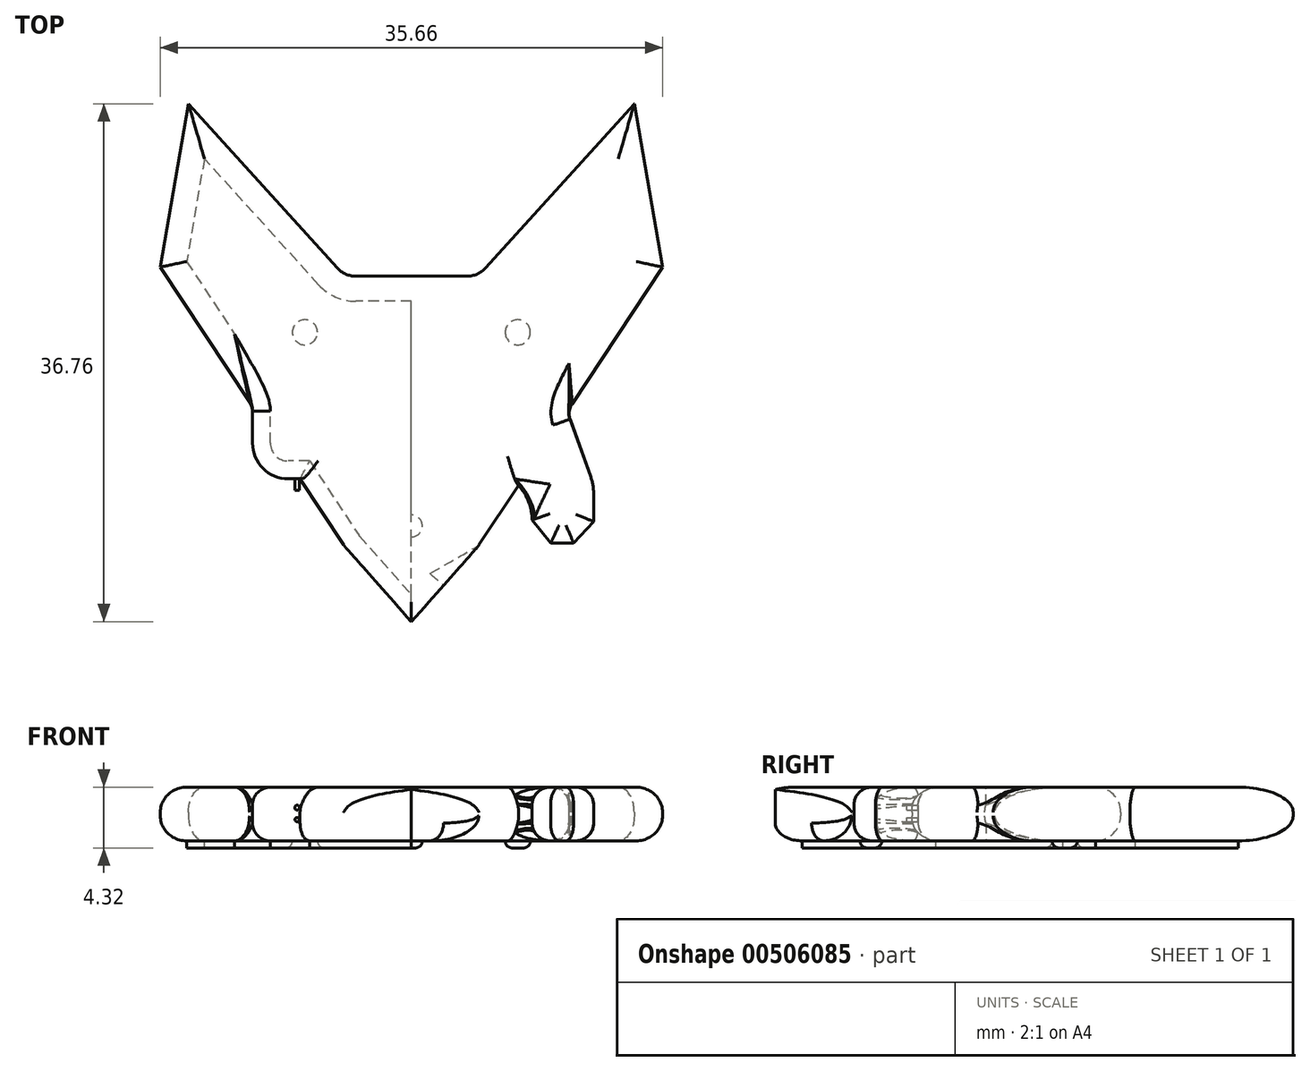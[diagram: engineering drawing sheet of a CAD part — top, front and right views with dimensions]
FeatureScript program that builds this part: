
annotation { "Feature Type Name" : "Feature", "Feature Type Description" : "" }
export const myFeature = defineFeature(function(context is Context, id is Id, definition is map)
    precondition{}
    {
        {
            var Q0;
            Q0=qCreatedBy(makeId("Top.planeOp"),FACE);
            var sketch = newSketch(context, id + "F0", { "sketchPlane" : qUnion([Q0])});
            skLineSegment(sketch, "E0.bottom", {"start": v(4.73, -9.6) * mm, "end": v(-4.73, -9.6) * mm});
            skLineSegment(sketch, "E0.top", {"start": v(4.73, 9.6) * mm, "end": v(-4.73, 9.6) * mm});
            skLineSegment(sketch, "E0.left", {"start": v(4.73, -9.6) * mm, "end": v(4.73, 9.6) * mm});
            skLineSegment(sketch, "E0.right", {"start": v(-4.73, -9.6) * mm, "end": v(-4.73, 9.6) * mm});
            skPoint(sketch, "E0.middle", {"position": v(0, 0) * mm});
            skLineSegment(sketch, "E1", {"start": v(-4.73, 9.6) * mm, "end": v(-15.82, 21.83) * mm});
            skLineSegment(sketch, "E2", {"start": v(-15.82, 21.83) * mm, "end": v(-17.83, 10.24) * mm});
            skLineSegment(sketch, "E3", {"start": v(-17.83, 10.24) * mm, "end": v(-4.73, -9.6) * mm});
            skLineSegment(sketch, "E4", {"start": v(-7.9, -4.79) * mm, "end": v(-11.28, -4.79) * mm});
            skPoint(sketch, "E4.endSnap0", {"position": v(-11.28, 0.33) * mm});
            skLineSegment(sketch, "E5", {"start": v(-11.28, -4.79) * mm, "end": v(-11.28, 0.33) * mm});
            skLineSegment(sketch, "E6", {"start": v(0, 17.28) * mm, "end": v(0, -14.93) * mm});
            skPoint(sketch, "E6.endSnap0", {"position": v(0, 9.6) * mm});
            skLineSegment(sketch, "E7.MirrorCS", {"start": v(4.73, 9.6) * mm, "end": v(15.82, 21.83) * mm});
            skLineSegment(sketch, "E8.MirrorCS", {"start": v(15.82, 21.83) * mm, "end": v(17.83, 10.24) * mm});
            skLineSegment(sketch, "E9.MirrorCS", {"start": v(17.83, 10.24) * mm, "end": v(4.73, -9.6) * mm});
            skCircle(sketch, "E10", {"center": v(0, -9.6) * mm, "radius": 4.73 * mm});
            skLineSegment(sketch, "E11", {"start": v(-4.73, -9.6) * mm, "end": v(0, -14.93) * mm});
            skLineSegment(sketch, "E12", {"start": v(0, -14.93) * mm, "end": v(4.73, -9.6) * mm});
            skLineSegment(sketch, "E13", {"start": v(11.06, 0) * mm, "end": v(12.94, -5.23) * mm});
            skLineSegment(sketch, "E14", {"start": v(12.94, -5.23) * mm, "end": v(12.94, -7.82) * mm});
            skLineSegment(sketch, "E15", {"start": v(12.94, -7.82) * mm, "end": v(11.52, -9.35) * mm});
            skLineSegment(sketch, "E16", {"start": v(11.52, -9.35) * mm, "end": v(9.88, -9.35) * mm});
            skLineSegment(sketch, "E17", {"start": v(9.88, -9.35) * mm, "end": v(8.57, -7.71) * mm});
            skLineSegment(sketch, "E18", {"start": v(8.57, -7.71) * mm, "end": v(8.57, -5.86) * mm});
            skLineSegment(sketch, "E19", {"start": v(8.57, -5.86) * mm, "end": v(7.61, -5.22) * mm});
            skSolve(sketch);
        }
        {
            var Q0;
            {var subQ0=sQuery(id+"F0.wireOp",EDGE,"E10");var subQ3=sQuery(id+"F0.wireOp",EDGE,"E6");var subQ5=makeQuery(id+"F0.imprint","INTERSECT",VERTEX,{"disambiguationData":[OD(0.0)],"derivedFrom":[subQ3,subQ0]});Q0=makeQuery(id+"F0.imprint","IMPRINT",FACE,{"disambiguationData":[TD([[makeQuery(id+"F0.imprint","IMPRINT",EDGE,{"disambiguationData":[TD([[subQ5,1.0]])],"derivedFrom":subQ3}),1.0]])]});}
            var Q1;
            {var subQ0=sQuery(id+"F0.wireOp",EDGE,"E10");var subQ3=sQuery(id+"F0.wireOp",EDGE,"E6");var subQ5=makeQuery(id+"F0.imprint","INTERSECT",VERTEX,{"disambiguationData":[OD(0.0)],"derivedFrom":[subQ3,subQ0]});Q1=makeQuery(id+"F0.imprint","IMPRINT",FACE,{"disambiguationData":[TD([[makeQuery(id+"F0.imprint","IMPRINT",EDGE,{"disambiguationData":[TD([[subQ5,1.0]])],"derivedFrom":subQ3}),-1.0]])]});}
            var Q2;
            {var subQ1=sQuery(id+"F0.wireOp",EDGE,"E0.bottom");var subQ3=sQuery(id+"F0.wireOp",EDGE,"E6");var subQ4=makeQuery(id+"F0.imprint","INTERSECT",VERTEX,{"derivedFrom":[subQ1,subQ3]});Q2=makeQuery(id+"F0.imprint","IMPRINT",FACE,{"disambiguationData":[TD([[makeQuery(id+"F0.imprint","IMPRINT",EDGE,{"disambiguationData":[TD([[subQ4,1.0]])],"derivedFrom":subQ3}),1.0]])]});}
            var Q3;
            {var subQ1=sQuery(id+"F0.wireOp",EDGE,"E0.bottom");var subQ3=sQuery(id+"F0.wireOp",EDGE,"E6");var subQ4=makeQuery(id+"F0.imprint","INTERSECT",VERTEX,{"derivedFrom":[subQ1,subQ3]});Q3=makeQuery(id+"F0.imprint","IMPRINT",FACE,{"disambiguationData":[TD([[makeQuery(id+"F0.imprint","IMPRINT",EDGE,{"disambiguationData":[TD([[subQ4,1.0]])],"derivedFrom":subQ3}),-1.0]])]});}
            var Q4;
            {var subQ0=sQuery(id+"F0.wireOp",EDGE,"E0.left");Q4=makeQuery(id+"F0.imprint","IMPRINT",FACE,{"disambiguationData":[TD([[makeQuery(id+"F0.imprint","IMPRINT",EDGE,{"derivedFrom":subQ0}),1.0]])]});}
            var Q5;
            {var subQ0=sQuery(id+"F0.wireOp",EDGE,"E0.right");Q5=makeQuery(id+"F0.imprint","IMPRINT",FACE,{"disambiguationData":[TD([[makeQuery(id+"F0.imprint","IMPRINT",EDGE,{"derivedFrom":subQ0}),-1.0]])]});}
            var Q6;
            {var subQ3=sQuery(id+"F0.wireOp",EDGE,"E0.right");Q6=makeQuery(id+"F0.imprint","IMPRINT",FACE,{"disambiguationData":[TD([[makeQuery(id+"F0.imprint","IMPRINT",EDGE,{"derivedFrom":subQ3}),1.0]])]});}
            var Q7;
            Q7=makeQuery(id+"F0.imprint","IMPRINT",FACE,{"disambiguationData":[TD([[makeQuery(id+"F0.imprint","IMPRINT",EDGE,{"derivedFrom":sQuery(id+"F0.wireOp",EDGE,"E0.left")}),-1.0]])]});
            var Q8;
            {var subQ2=sQuery(id+"F0.wireOp",EDGE,"E0.bottom");var subQ4=sQuery(id+"F0.wireOp",EDGE,"E6");var subQ5=makeQuery(id+"F0.imprint","INTERSECT",VERTEX,{"derivedFrom":[subQ2,subQ4]});Q8=makeQuery(id+"F0.imprint","IMPRINT",FACE,{"disambiguationData":[TD([[makeQuery(id+"F0.imprint","IMPRINT",EDGE,{"disambiguationData":[TD([[subQ5,-1.0]])],"derivedFrom":subQ4}),-1.0]])]});}
            var Q9;
            {var subQ2=sQuery(id+"F0.wireOp",EDGE,"E0.bottom");var subQ4=sQuery(id+"F0.wireOp",EDGE,"E6");var subQ5=makeQuery(id+"F0.imprint","INTERSECT",VERTEX,{"derivedFrom":[subQ2,subQ4]});Q9=makeQuery(id+"F0.imprint","IMPRINT",FACE,{"disambiguationData":[TD([[makeQuery(id+"F0.imprint","IMPRINT",EDGE,{"disambiguationData":[TD([[subQ5,-1.0]])],"derivedFrom":subQ4}),1.0]])]});}
            var Q10;
            {var subQ0=sQuery(id+"F0.wireOp",EDGE,"E12");var subQ3=sQuery(id+"F0.wireOp",EDGE,"E10");var subQ5=makeQuery(id+"F0.imprint","INTERSECT",VERTEX,{"derivedFrom":[subQ3,subQ0]});Q10=makeQuery(id+"F0.imprint","IMPRINT",FACE,{"disambiguationData":[TD([[makeQuery(id+"F0.imprint","IMPRINT",EDGE,{"disambiguationData":[TD([[subQ5,1.0]])],"derivedFrom":subQ3}),-1.0]])]});}
            var Q11;
            {var subQ0=sQuery(id+"F0.wireOp",EDGE,"E11");var subQ3=sQuery(id+"F0.wireOp",EDGE,"E10");var subQ5=makeQuery(id+"F0.imprint","INTERSECT",VERTEX,{"derivedFrom":[subQ3,subQ0]});Q11=makeQuery(id+"F0.imprint","IMPRINT",FACE,{"disambiguationData":[TD([[makeQuery(id+"F0.imprint","IMPRINT",EDGE,{"disambiguationData":[TD([[subQ5,-1.0]])],"derivedFrom":subQ3}),-1.0]])]});}
            var Q12;
            {var subQ0=sQuery(id+"F0.wireOp",EDGE,"E13");Q12=makeQuery(id+"F0.imprint","IMPRINT",FACE,{"disambiguationData":[TD([[makeQuery(id+"F0.imprint","IMPRINT",EDGE,{"derivedFrom":subQ0}),-1.0]])]});}
            extrude(context, id + "F1", {"entities" : qUnion([Q0, Q1, Q2, Q3, Q4, Q5, Q6, Q7, Q8, Q9, Q10, Q11, Q12]), "depth" : 3.8 * mm});
        }
        {
            var Q0;
            {var subQ0=sQuery(id+"F0.wireOp",EDGE,"E4");Q0=makeQuery(id+"F0.imprint","IMPRINT",FACE,{"disambiguationData":[TD([[makeQuery(id+"F0.imprint","IMPRINT",EDGE,{"derivedFrom":subQ0}),-1.0]])]});}
            extrude(context, id + "F2", {"entities" : qUnion([Q0]), "operationType" : NewBodyOperationType.ADD, "depth" : 3.8 * mm});
        }
        {
            var Q0;
            Q0=makeQuery(id+"F1.opExtrude","CAP_EDGE",EDGE,{"disambiguationData":[OSD([sQuery(id+"F0.wireOp",EDGE,"E0.top")])],"isStart":false});
            var Q1;
            Q1=makeQuery(id+"F1.opExtrude","CAP_EDGE",EDGE,{"disambiguationData":[OSD([sQuery(id+"F0.wireOp",EDGE,"E0.top")])],"isStart":true});
            var Q2;
            Q2=makeQuery(id+"F1.opExtrude","CAP_EDGE",EDGE,{"disambiguationData":[OSD([sQuery(id+"F0.wireOp",EDGE,"E1")])],"isStart":false});
            var Q3;
            Q3=makeQuery(id+"F1.opExtrude","CAP_EDGE",EDGE,{"disambiguationData":[OSD([sQuery(id+"F0.wireOp",EDGE,"E1")])],"isStart":true});
            var Q4;
            Q4=makeQuery(id+"F1.opExtrude","CAP_EDGE",EDGE,{"disambiguationData":[OSD([sQuery(id+"F0.wireOp",EDGE,"E7.MirrorCS")])],"isStart":false});
            var Q5;
            Q5=makeQuery(id+"F1.opExtrude","CAP_EDGE",EDGE,{"disambiguationData":[OSD([sQuery(id+"F0.wireOp",EDGE,"E7.MirrorCS")])],"isStart":true});
            var Q6;
            Q6=makeQuery(id+"F1.opExtrude","CAP_EDGE",EDGE,{"disambiguationData":[OSD([sQuery(id+"F0.wireOp",EDGE,"E2")])],"isStart":false});
            var Q7;
            Q7=makeQuery(id+"F1.opExtrude","CAP_EDGE",EDGE,{"disambiguationData":[OSD([sQuery(id+"F0.wireOp",EDGE,"E2")])],"isStart":true});
            var Q8;
            Q8=makeQuery(id+"F1.opExtrude","CAP_EDGE",EDGE,{"disambiguationData":[OSD([sQuery(id+"F0.wireOp",EDGE,"E3")])],"isStart":false});
            var Q9;
            {var subQ1=sQuery(id+"F0.wireOp",EDGE,"E3");var subQ2=sQuery(id+"F0.wireOp",EDGE,"E2");Q9=makeQuery(id+"F2.boolean.opBoolean","SPLIT",EDGE,{"disambiguationData":[TD([makeQuery(id+"F1.opExtrude","SWEPT_FACE",FACE,{"disambiguationData":[OSD([subQ2])]})])],"derivedFrom":makeQuery(id+"F1.opExtrude","CAP_EDGE",EDGE,{"disambiguationData":[OSD([subQ1])],"isStart":true})});}
            var Q10;
            {var subQ1=sQuery(id+"F0.wireOp",EDGE,"E3");var subQ2=sQuery(id+"F0.wireOp",EDGE,"E10");Q10=makeQuery(id+"F2.boolean.opBoolean","SPLIT",EDGE,{"disambiguationData":[TD([makeQuery(id+"F1.opExtrude","SWEPT_FACE",FACE,{"disambiguationData":[OSD([subQ2])]})])],"derivedFrom":makeQuery(id+"F1.opExtrude","CAP_EDGE",EDGE,{"disambiguationData":[OSD([subQ1])],"isStart":true})});}
            var Q11;
            Q11=makeQuery(id+"F1.opExtrude","CAP_EDGE",EDGE,{"disambiguationData":[OSD([sQuery(id+"F0.wireOp",EDGE,"E9.MirrorCS")])],"isStart":false});
            var Q12;
            Q12=makeQuery(id+"F1.opExtrude","CAP_EDGE",EDGE,{"disambiguationData":[OSD([sQuery(id+"F0.wireOp",EDGE,"E9.MirrorCS")])],"isStart":true});
            var Q13;
            Q13=makeQuery(id+"F1.opExtrude","CAP_EDGE",EDGE,{"disambiguationData":[OSD([sQuery(id+"F0.wireOp",EDGE,"E8.MirrorCS")])],"isStart":false});
            var Q14;
            Q14=makeQuery(id+"F1.opExtrude","CAP_EDGE",EDGE,{"disambiguationData":[OSD([sQuery(id+"F0.wireOp",EDGE,"E8.MirrorCS")])],"isStart":true});
            var Q15;
            Q15=makeQuery(id+"F1.opExtrude","SWEPT_EDGE",EDGE,{"disambiguationData":[OSD([sQuery(id+"F0.wireOp",EDGE,"E0.top"),sQuery(id+"F0.wireOp",EDGE,"E0.right"),sQuery(id+"F0.wireOp",EDGE,"E1")])]});
            var Q16;
            Q16=makeQuery(id+"F1.opExtrude","SWEPT_EDGE",EDGE,{"disambiguationData":[OSD([sQuery(id+"F0.wireOp",EDGE,"E0.top"),sQuery(id+"F0.wireOp",EDGE,"E0.left"),sQuery(id+"F0.wireOp",EDGE,"E7.MirrorCS")])]});
            var Q17;
            Q17=makeQuery(id+"F1.opExtrude","SWEPT_EDGE",EDGE,{"disambiguationData":[OSD([sQuery(id+"F0.wireOp",EDGE,"E0.bottom"),sQuery(id+"F0.wireOp",EDGE,"E0.left"),sQuery(id+"F0.wireOp",EDGE,"E9.MirrorCS"),sQuery(id+"F0.wireOp",EDGE,"E10")])]});
            var Q18;
            Q18=makeQuery(id+"F1.opExtrude","SWEPT_EDGE",EDGE,{"disambiguationData":[OSD([sQuery(id+"F0.wireOp",EDGE,"E0.bottom"),sQuery(id+"F0.wireOp",EDGE,"E0.right"),sQuery(id+"F0.wireOp",EDGE,"E3"),sQuery(id+"F0.wireOp",EDGE,"E10")])]});
            fillet(context, id + "F3", {"entities" : qUnion([Q0, Q1, Q2, Q3, Q4, Q5, Q6, Q7, Q8, Q9, Q10, Q11, Q12, Q13, Q14, Q15, Q16, Q17, Q18]), "radius" : 1.78 * mm, "tangentPropagation" : true, "allowEdgeOverflow" : false});
        }
        {
            var Q0;
            Q0=makeQuery(id+"F2.opExtrude","SWEPT_EDGE",EDGE,{"disambiguationData":[OSD([sQuery(id+"F0.wireOp",EDGE,"E4"),sQuery(id+"F0.wireOp",EDGE,"E5")])]});
            fillet(context, id + "F4", {"entities" : qUnion([Q0]), "radius" : 2.54 * mm, "tangentPropagation" : true, "allowEdgeOverflow" : false});
        }
        {
            var Q0;
            Q0=makeQuery(id+"F2.opExtrude","CAP_EDGE",EDGE,{"disambiguationData":[OSD([sQuery(id+"F0.wireOp",EDGE,"E5")])],"isStart":false});
            var Q1;
            Q1=makeQuery(id+"F2.opExtrude","CAP_EDGE",EDGE,{"disambiguationData":[OSD([sQuery(id+"F0.wireOp",EDGE,"E5")])],"isStart":true});
            var Q2;
            Q2=makeQuery(id+"F2.opExtrude","CAP_EDGE",EDGE,{"disambiguationData":[OSD([sQuery(id+"F0.wireOp",EDGE,"E5")])],"isStart":true});
            var Q3;
            Q3=makeQuery(id+"F2.opExtrude","CAP_EDGE",EDGE,{"disambiguationData":[OSD([sQuery(id+"F0.wireOp",EDGE,"E4")])],"isStart":false});
            var Q4;
            Q4=makeQuery(id+"F2.opExtrude","SWEPT_EDGE",EDGE,{"disambiguationData":[OSD([sQuery(id+"F0.wireOp",EDGE,"E3"),sQuery(id+"F0.wireOp",EDGE,"E5")])]});
            var Q5;
            Q5=makeQuery(id+"F2.opExtrude","SWEPT_EDGE",EDGE,{"disambiguationData":[OSD([sQuery(id+"F0.wireOp",EDGE,"E3"),sQuery(id+"F0.wireOp",EDGE,"E4")])]});
            var Q6;
            Q6=makeQuery(id+"F2.opExtrude","CAP_EDGE",EDGE,{"disambiguationData":[OSD([sQuery(id+"F0.wireOp",EDGE,"E4")])],"isStart":true});
            var Q7;
            Q7=makeQuery(id+"F1.opExtrude","CAP_EDGE",EDGE,{"disambiguationData":[OSD([sQuery(id+"F0.wireOp",EDGE,"E11")])],"isStart":true});
            var Q8;
            Q8=makeQuery(id+"F3.opFillet","BLEND_EDGE",EDGE,{"blendedFrom":[makeQuery(id+"F1.opExtrude","CAP_EDGE",EDGE,{"disambiguationData":[OSD([sQuery(id+"F0.wireOp",EDGE,"E9.MirrorCS")])],"isStart":true}),makeQuery(id+"F1.opExtrude","SWEPT_FACE",FACE,{"disambiguationData":[OSD([sQuery(id+"F0.wireOp",EDGE,"E12")])]})],"blendedInto":[makeQuery(id+"F1.opExtrude","SWEPT_FACE",FACE,{"disambiguationData":[OSD([sQuery(id+"F0.wireOp",EDGE,"E12")])]})]});
            fillet(context, id + "F5", {"entities" : qUnion([Q0, Q1, Q2, Q3, Q4, Q5, Q6, Q7, Q8]), "radius" : 1.27 * mm, "tangentPropagation" : true, "allowEdgeOverflow" : false});
        }
        {
            var Q0;
            Q0=qCreatedBy(makeId("Front.planeOp"),FACE);
            var sketch = newSketch(context, id + "F6", { "sketchPlane" : qUnion([Q0])});
            skCircle(sketch, "E20", {"center": v(-8.1, 2.36) * mm, "radius": 0.17 * mm});
            skCircle(sketch, "E21", {"center": v(-8.1, 1.51) * mm, "radius": 0.15 * mm});
            skSolve(sketch);
        }
        {
            var Q0;
            Q0 = qSketchRegion(id + "F6", true);
            extrude(context, id + "F7", {"entities" : qUnion([Q0]), "operationType" : NewBodyOperationType.ADD, "depth" : 5.6 * mm});
        }
        {
            var Q0;
            Q0=makeQuery(id+"F1.opExtrude","CAP_EDGE",EDGE,{"disambiguationData":[OSD([sQuery(id+"F0.wireOp",EDGE,"E19")])],"isStart":false});
            var Q1;
            Q1=makeQuery(id+"F1.opExtrude","CAP_EDGE",EDGE,{"disambiguationData":[OSD([sQuery(id+"F0.wireOp",EDGE,"E19")])],"isStart":true});
            var Q2;
            Q2=makeQuery(id+"F1.opExtrude","CAP_EDGE",EDGE,{"disambiguationData":[OSD([sQuery(id+"F0.wireOp",EDGE,"E13")])],"isStart":false});
            var Q3;
            Q3=makeQuery(id+"F1.opExtrude","CAP_EDGE",EDGE,{"disambiguationData":[OSD([sQuery(id+"F0.wireOp",EDGE,"E13")])],"isStart":true});
            var Q4;
            Q4=makeQuery(id+"F1.opExtrude","SWEPT_EDGE",EDGE,{"disambiguationData":[OSD([sQuery(id+"F0.wireOp",EDGE,"E9.MirrorCS"),sQuery(id+"F0.wireOp",EDGE,"E13")])]});
            var Q5;
            Q5=makeQuery(id+"F1.opExtrude","CAP_EDGE",EDGE,{"disambiguationData":[OSD([sQuery(id+"F0.wireOp",EDGE,"E16")])],"isStart":true});
            var Q6;
            Q6=makeQuery(id+"F1.opExtrude","CAP_EDGE",EDGE,{"disambiguationData":[OSD([sQuery(id+"F0.wireOp",EDGE,"E15")])],"isStart":true});
            var Q7;
            Q7=makeQuery(id+"F1.opExtrude","CAP_EDGE",EDGE,{"disambiguationData":[OSD([sQuery(id+"F0.wireOp",EDGE,"E15")])],"isStart":false});
            var Q8;
            Q8=makeQuery(id+"F1.opExtrude","CAP_EDGE",EDGE,{"disambiguationData":[OSD([sQuery(id+"F0.wireOp",EDGE,"E16")])],"isStart":false});
            var Q9;
            Q9=makeQuery(id+"F1.opExtrude","CAP_EDGE",EDGE,{"disambiguationData":[OSD([sQuery(id+"F0.wireOp",EDGE,"E18")])],"isStart":false});
            var Q10;
            Q10=makeQuery(id+"F1.opExtrude","CAP_EDGE",EDGE,{"disambiguationData":[OSD([sQuery(id+"F0.wireOp",EDGE,"E18")])],"isStart":true});
            var Q11;
            Q11=makeQuery(id+"F1.opExtrude","CAP_EDGE",EDGE,{"disambiguationData":[OSD([sQuery(id+"F0.wireOp",EDGE,"E17")])],"isStart":true});
            var Q12;
            Q12=makeQuery(id+"F1.opExtrude","CAP_EDGE",EDGE,{"disambiguationData":[OSD([sQuery(id+"F0.wireOp",EDGE,"E17")])],"isStart":false});
            var Q13;
            Q13=makeQuery(id+"F1.opExtrude","CAP_EDGE",EDGE,{"disambiguationData":[OSD([sQuery(id+"F0.wireOp",EDGE,"E14")])],"isStart":false});
            var Q14;
            Q14=makeQuery(id+"F1.opExtrude","CAP_EDGE",EDGE,{"disambiguationData":[OSD([sQuery(id+"F0.wireOp",EDGE,"E14")])],"isStart":true});
            fillet(context, id + "F8", {"entities" : qUnion([Q0, Q1, Q2, Q3, Q4, Q5, Q6, Q7, Q8, Q9, Q10, Q11, Q12, Q13, Q14]), "radius" : 1.27 * mm, "tangentPropagation" : true, "allowEdgeOverflow" : false});
        }
        {
            var Q0;
            Q0=makeQuery(id+"F1.opExtrude","SWEPT_EDGE",EDGE,{"disambiguationData":[OSD([sQuery(id+"F0.wireOp",EDGE,"E13"),sQuery(id+"F0.wireOp",EDGE,"E14")])]});
            var Q1;
            Q1=makeQuery(id+"F1.opExtrude","SWEPT_EDGE",EDGE,{"disambiguationData":[OSD([sQuery(id+"F0.wireOp",EDGE,"E18"),sQuery(id+"F0.wireOp",EDGE,"E19")])]});
            fillet(context, id + "F9", {"entities" : qUnion([Q0, Q1]), "radius" : 3.8 * mm, "tangentPropagation" : true, "allowEdgeOverflow" : false});
        }
        {
            var Q0;
            {var subQ0=sQuery(id+"F0.wireOp",EDGE,"E3");Q0=makeQuery(id+"F2.boolean.opBoolean","MERGE",FACE,{"derivedFrom":[makeQuery(id+"F1.opExtrude","CAP_FACE",FACE,{"disambiguationData":[OSD([sQuery(id+"F0.wireOp",EDGE,"E0.top"),sQuery(id+"F0.wireOp",EDGE,"E1"),sQuery(id+"F0.wireOp",EDGE,"E2"),subQ0,sQuery(id+"F0.wireOp",EDGE,"E7.MirrorCS"),sQuery(id+"F0.wireOp",EDGE,"E8.MirrorCS"),sQuery(id+"F0.wireOp",EDGE,"E9.MirrorCS"),sQuery(id+"F0.wireOp",EDGE,"E11"),sQuery(id+"F0.wireOp",EDGE,"E12"),sQuery(id+"F0.wireOp",EDGE,"E13"),sQuery(id+"F0.wireOp",EDGE,"E14"),sQuery(id+"F0.wireOp",EDGE,"E15"),sQuery(id+"F0.wireOp",EDGE,"E16"),sQuery(id+"F0.wireOp",EDGE,"E17"),sQuery(id+"F0.wireOp",EDGE,"E18"),sQuery(id+"F0.wireOp",EDGE,"E19")])],"isStart":true}),makeQuery(id+"F2.opExtrude","CAP_FACE",FACE,{"disambiguationData":[OSD([subQ0,sQuery(id+"F0.wireOp",EDGE,"E4"),sQuery(id+"F0.wireOp",EDGE,"E5")])],"isStart":true})]});}
            var sketch = newSketch(context, id + "F10", { "sketchPlane" : qUnion([Q0])});
            skCircle(sketch, "E22", {"center": v(0, 8.14) * mm, "radius": 0.78 * mm});
            skCircle(sketch, "E23", {"center": v(7.55, -5.62) * mm, "radius": 0.9 * mm});
            skLineSegment(sketch, "E24", {"start": v(0, 13.02) * mm, "end": v(0, -18.53) * mm});
            skPoint(sketch, "E24.endSnap0", {"position": v(0, -7.81) * mm});
            skCircle(sketch, "E25.MirrorC", {"center": v(-7.55, -5.62) * mm, "radius": 0.9 * mm});
            skSolve(sketch);
        }
        {
            var Q0;
            Q0=makeQuery(id+"F10.imprint","IMPRINT",FACE,{"disambiguationData":[TD([[makeQuery(id+"F10.imprint","IMPRINT",EDGE,{"derivedFrom":sQuery(id+"F10.wireOp",EDGE,"E23")}),1.0]])]});
            var Q1;
            Q1=makeQuery(id+"F10.imprint","IMPRINT",FACE,{"disambiguationData":[TD([[makeQuery(id+"F10.imprint","IMPRINT",EDGE,{"derivedFrom":sQuery(id+"F10.wireOp",EDGE,"E25.MirrorC")}),-1.0]])]});
            var Q2;
            {var subQ0=sQuery(id+"F10.wireOp",EDGE,"E24");var subQ1=sQuery(id+"F10.wireOp",EDGE,"E22");var subQ2=makeQuery(id+"F10.imprint","INTERSECT",VERTEX,{"disambiguationData":[OD(0.0)],"derivedFrom":[subQ1,subQ0]});Q2=makeQuery(id+"F10.imprint","IMPRINT",FACE,{"disambiguationData":[TD([[makeQuery(id+"F10.imprint","IMPRINT",EDGE,{"disambiguationData":[TD([[subQ2,1.0]])],"derivedFrom":subQ1}),1.0]])]});}
            var Q3;
            {var subQ0=sQuery(id+"F10.wireOp",EDGE,"E24");var subQ1=sQuery(id+"F10.wireOp",EDGE,"E22");var subQ2=makeQuery(id+"F10.imprint","INTERSECT",VERTEX,{"disambiguationData":[OD(0.0)],"derivedFrom":[subQ1,subQ0]});Q3=makeQuery(id+"F10.imprint","IMPRINT",FACE,{"disambiguationData":[TD([[makeQuery(id+"F10.imprint","IMPRINT",EDGE,{"disambiguationData":[TD([[subQ2,-1.0]])],"derivedFrom":subQ1}),1.0]])]});}
            extrude(context, id + "F11", {"entities" : qUnion([Q0, Q1, Q2, Q3]), "operationType" : NewBodyOperationType.ADD, "depth" : 0.5 * mm});
        }
        {
            var Q0;
            Q0=makeQuery(id+"F11.opExtrude","CAP_EDGE",EDGE,{"disambiguationData":[OSD([sQuery(id+"F10.wireOp",EDGE,"E25.MirrorC")])],"isStart":false});
            var Q1;
            Q1=makeQuery(id+"F11.opExtrude","CAP_EDGE",EDGE,{"disambiguationData":[OSD([sQuery(id+"F10.wireOp",EDGE,"E23")])],"isStart":false});
            var Q2;
            Q2=makeQuery(id+"F11.opExtrude","CAP_EDGE",EDGE,{"disambiguationData":[OSD([sQuery(id+"F10.wireOp",EDGE,"E22")])],"isStart":false});
            fillet(context, id + "F12", {"entities" : qUnion([Q0, Q1, Q2]), "radius" : 0.5 * mm, "tangentPropagation" : true, "allowEdgeOverflow" : false});
        }
    });
